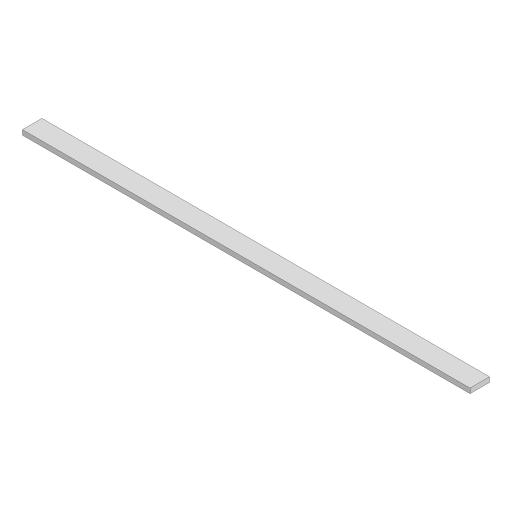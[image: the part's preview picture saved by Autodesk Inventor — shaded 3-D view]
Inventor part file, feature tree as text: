
AUTODESK INVENTOR PART (.ipt)
format: ipt  version: 2024 (Build 280153000, 153)  size: 83,968 bytes
history: native  units: in
note: dims shown in document units (in); Inventor stores cm internally (conversion verified against a paired STEP export)
features: extrude x1, sketch x1
ambient origin geometry x8: Origin, YZ Plane, XZ Plane, XY Plane, X Axis, Y Axis, Z Axis, Center Point
bodies: Solid1 (feature_tree)
feature tree (2):
  extrude  "Extrusion1"  Depth=10.315in
  sketch  "Sketch1"  dims[d0=2.5591in d1=10.315in d2=236.2205in d3=0.0in d4=0.0197in d5=0.0344in d6=0.0197in d7=0.0344in]
